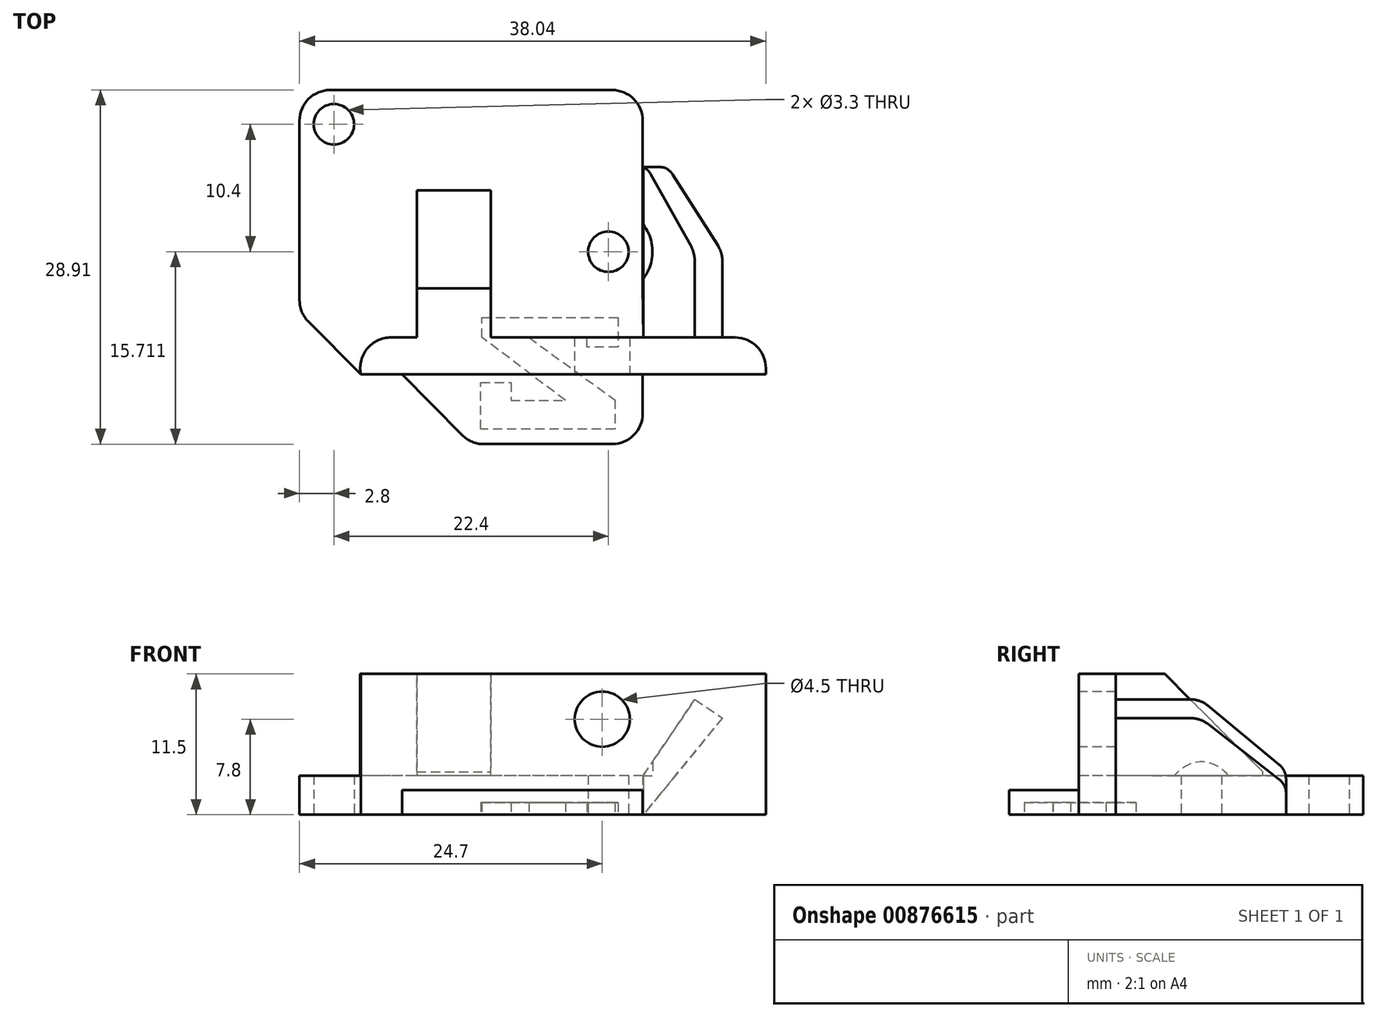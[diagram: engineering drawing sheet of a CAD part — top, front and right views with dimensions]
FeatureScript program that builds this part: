
annotation { "Feature Type Name" : "Feature", "Feature Type Description" : "" }
export const myFeature = defineFeature(function(context is Context, id is Id, definition is map)
    precondition{}
    {
        {
            var Q0;
            Q0=qCreatedBy(makeId("Top.planeOp"),FACE);
            var sketch = newSketch(context, id + "F0", { "sketchPlane" : qUnion([Q0])});
            skLineSegment(sketch, "E0.bottom", {"start": v(0, -51.12) * mm, "end": v(0, 0) * mm});
            skLineSegment(sketch, "E0.top", {"start": v(28, -51.12) * mm, "end": v(28, 0) * mm});
            skLineSegment(sketch, "E0.left", {"start": v(0, -51.12) * mm, "end": v(28, -51.12) * mm});
            skLineSegment(sketch, "E1", {"start": v(28, -35.12) * mm, "end": v(0, -35.12) * mm});
            skCircle(sketch, "E2", {"center": v(2.8, -37.92) * mm, "radius": 1.65 * mm});
            skCircle(sketch, "E3", {"center": v(25.2, -48.32) * mm, "radius": 1.65 * mm});
            skLineSegment(sketch, "E4.top", {"start": v(0, -58.32) * mm, "end": v(28, -58.32) * mm});
            skLineSegment(sketch, "E4.left", {"start": v(0, -51.12) * mm, "end": v(0, -58.32) * mm});
            skLineSegment(sketch, "E5", {"start": v(8.36, -58.32) * mm, "end": v(13.99, -64.03) * mm});
            skLineSegment(sketch, "E6", {"start": v(13.99, -64.03) * mm, "end": v(28, -64.03) * mm});
            skLineSegment(sketch, "E7", {"start": v(28, -64.03) * mm, "end": v(28, -58.32) * mm});
            skLineSegment(sketch, "E8", {"start": v(28.04, -55.32) * mm, "end": v(0, -55.32) * mm});
            skLineSegment(sketch, "E9", {"start": v(28, -51.12) * mm, "end": v(28.04, -55.32) * mm});
            skLineSegment(sketch, "E10", {"start": v(28.04, -55.32) * mm, "end": v(38.04, -55.32) * mm});
            skLineSegment(sketch, "E11", {"start": v(38.04, -55.32) * mm, "end": v(38.04, -58.32) * mm});
            skLineSegment(sketch, "E12", {"start": v(38.04, -58.32) * mm, "end": v(28, -58.32) * mm});
            skSolve(sketch);
        }
        {
            var Q0;
            {var subQ0=sQuery(id+"F0.wireOp",EDGE,"E1");Q0=makeQuery(id+"F0.imprint","IMPRINT",FACE,{"disambiguationData":[TD([[makeQuery(id+"F0.imprint","IMPRINT",EDGE,{"derivedFrom":subQ0}),1.0]])]});}
            var Q1;
            {var subQ0=sQuery(id+"F0.wireOp",EDGE,"E0.left");Q1=makeQuery(id+"F0.imprint","IMPRINT",FACE,{"disambiguationData":[TD([[makeQuery(id+"F0.imprint","IMPRINT",EDGE,{"derivedFrom":subQ0}),-1.0]])]});}
            extrude(context, id + "F1", {"entities" : qUnion([Q0, Q1]), "depth" : 3.2 * mm, "offsetDistance" : 25 * mm});
        }
        {
            var Q0;
            {var subQ3=sQuery(id+"F0.wireOp",EDGE,"E8");Q0=makeQuery(id+"F0.imprint","IMPRINT",FACE,{"disambiguationData":[TD([[makeQuery(id+"F0.imprint","IMPRINT",EDGE,{"derivedFrom":subQ3}),1.0]])]});}
            extrude(context, id + "F2", {"entities" : qUnion([Q0]), "operationType" : NewBodyOperationType.ADD, "depth" : 11.5 * mm, "offsetDistance" : 25 * mm});
        }
        {
            var Q0;
            {var subQ2=sQuery(id+"F0.wireOp",EDGE,"E5");Q0=makeQuery(id+"F0.imprint","IMPRINT",FACE,{"disambiguationData":[TD([[makeQuery(id+"F0.imprint","IMPRINT",EDGE,{"derivedFrom":subQ2}),1.0]])]});}
            extrude(context, id + "F3", {"entities" : qUnion([Q0]), "operationType" : NewBodyOperationType.ADD, "depth" : 2 * mm, "offsetDistance" : 25 * mm});
        }
        {
            var Q0;
            Q0=makeQuery(id+"F2.opExtrude","SWEPT_FACE",FACE,{"disambiguationData":[OSD([sQuery(id+"F0.wireOp",EDGE,"E4.top")])]});
            var sketch = newSketch(context, id + "F4", { "sketchPlane" : qUnion([Q0])});
            skCircle(sketch, "E13", {"center": v(24.7, 7.8) * mm, "radius": 2.25 * mm});
            skSolve(sketch);
        }
        {
            var Q0;
            {var subQ0=sQuery(id+"F4.wireOp",EDGE,"E13");var subQ1=makeQuery(id+"F2.opExtrude","CAP_EDGE",EDGE,{"disambiguationData":[OSD([sQuery(id+"F0.wireOp",EDGE,"E4.top")])],"isStart":false});var subQ2=makeQuery(id+"F4.imprint","INTERSECT",VERTEX,{"disambiguationData":[OD(0.0)],"derivedFrom":[subQ1,subQ0]});Q0=makeQuery(id+"F4.imprint","IMPRINT",FACE,{"disambiguationData":[TD([[makeQuery(id+"F4.imprint","IMPRINT",EDGE,{"disambiguationData":[TD([[subQ2,1.0]])],"derivedFrom":subQ0}),1.0]])]});}
            var Q1;
            {var subQ0=sQuery(id+"F4.wireOp",EDGE,"E13");var subQ1=makeQuery(id+"F2.opExtrude","CAP_EDGE",EDGE,{"disambiguationData":[OSD([sQuery(id+"F0.wireOp",EDGE,"E4.top")])],"isStart":false});var subQ2=makeQuery(id+"F4.imprint","INTERSECT",VERTEX,{"disambiguationData":[OD(0.0)],"derivedFrom":[subQ1,subQ0]});Q1=makeQuery(id+"F4.imprint","IMPRINT",FACE,{"disambiguationData":[TD([[makeQuery(id+"F4.imprint","IMPRINT",EDGE,{"disambiguationData":[TD([[subQ2,-1.0]])],"derivedFrom":subQ0}),1.0]])]});}
            extrude(context, id + "F5", {"entities" : qUnion([Q0, Q1]), "operationType" : NewBodyOperationType.REMOVE, "oppositeDirection" : true, "depth" : 25 * mm, "offsetDistance" : 25 * mm});
        }
        {
            var Q0;
            Q0=makeQuery(id+"F2.opExtrude","SWEPT_EDGE",EDGE,{"disambiguationData":[OSD([sQuery(id+"F0.wireOp",EDGE,"E4.top"),sQuery(id+"F0.wireOp",EDGE,"E4.left")])]});
            chamfer(context, id + "F6", {"entities" : qUnion([Q0]), "width" : 5 * mm, "tangentPropagation" : true});
        }
        {
            var Q0;
            Q0=makeQuery(id+"F6.opChamfer","BLEND_EDGE",EDGE,{"blendedFrom":[makeQuery(id+"F2.opExtrude","SWEPT_EDGE",EDGE,{"disambiguationData":[OSD([sQuery(id+"F0.wireOp",EDGE,"E4.top"),sQuery(id+"F0.wireOp",EDGE,"E4.left")])]}),makeQuery(id+"F2.opExtrude","SWEPT_FACE",FACE,{"disambiguationData":[OSD([sQuery(id+"F0.wireOp",EDGE,"E8")])]})],"blendedInto":[makeQuery(id+"F2.opExtrude","SWEPT_FACE",FACE,{"disambiguationData":[OSD([sQuery(id+"F0.wireOp",EDGE,"E8")])]})]});
            var Q1;
            {var subQ0=sQuery(id+"F0.wireOp",EDGE,"E4.left");Q1=makeQuery(id+"F6.opChamfer","BLEND_EDGE",EDGE,{"blendedFrom":[makeQuery(id+"F2.opExtrude","SWEPT_EDGE",EDGE,{"disambiguationData":[OSD([sQuery(id+"F0.wireOp",EDGE,"E4.top"),subQ0])]}),makeQuery(id+"F2.boolean.opBoolean","MERGE",FACE,{"derivedFrom":[makeQuery(id+"F1.opExtrude","SWEPT_FACE",FACE,{"disambiguationData":[OSD([sQuery(id+"F0.wireOp",EDGE,"E0.bottom"),subQ0])]}),makeQuery(id+"F2.opExtrude","SWEPT_FACE",FACE,{"disambiguationData":[OSD([subQ0])]})]})],"blendedInto":[makeQuery(id+"F2.boolean.opBoolean","MERGE",FACE,{"derivedFrom":[makeQuery(id+"F1.opExtrude","SWEPT_FACE",FACE,{"disambiguationData":[OSD([sQuery(id+"F0.wireOp",EDGE,"E0.bottom"),subQ0])]}),makeQuery(id+"F2.opExtrude","SWEPT_FACE",FACE,{"disambiguationData":[OSD([subQ0])]})]})]});}
            var Q2;
            Q2=makeQuery(id+"F3.opExtrude","SWEPT_EDGE",EDGE,{"disambiguationData":[OSD([sQuery(id+"F0.wireOp",EDGE,"E5"),sQuery(id+"F0.wireOp",EDGE,"E6")])]});
            var Q3;
            Q3=makeQuery(id+"F3.opExtrude","SWEPT_EDGE",EDGE,{"disambiguationData":[OSD([sQuery(id+"F0.wireOp",EDGE,"E6"),sQuery(id+"F0.wireOp",EDGE,"E7")])]});
            var Q4;
            Q4=makeQuery(id+"F1.opExtrude","SWEPT_EDGE",EDGE,{"disambiguationData":[OSD([sQuery(id+"F0.wireOp",EDGE,"E0.top"),sQuery(id+"F0.wireOp",EDGE,"E1")])]});
            var Q5;
            Q5=makeQuery(id+"F1.opExtrude","SWEPT_EDGE",EDGE,{"disambiguationData":[OSD([sQuery(id+"F0.wireOp",EDGE,"E0.bottom"),sQuery(id+"F0.wireOp",EDGE,"E1")])]});
            var Q6;
            Q6=makeQuery(id+"F3.opExtrude","SWEPT_EDGE",EDGE,{"disambiguationData":[OSD([sQuery(id+"F0.wireOp",EDGE,"E4.top"),sQuery(id+"F0.wireOp",EDGE,"E5")])]});
            var Q7;
            Q7=makeQuery(id+"F2.opExtrude","SWEPT_EDGE",EDGE,{"disambiguationData":[OSD([sQuery(id+"F0.wireOp",EDGE,"E10"),sQuery(id+"F0.wireOp",EDGE,"E11")])]});
            fillet(context, id + "F7", {"entities" : qUnion([Q0, Q1, Q2, Q3, Q4, Q5, Q6, Q7]), "radius" : 2.5 * mm, "tangentPropagation" : true, "allowEdgeOverflow" : false});
        }
        {
            var Q0;
            Q0=makeQuery(id+"F2.opExtrude","SWEPT_FACE",FACE,{"disambiguationData":[OSD([sQuery(id+"F0.wireOp",EDGE,"E8"),sQuery(id+"F0.wireOp",EDGE,"E10")])]});
            var sketch = newSketch(context, id + "F8", { "sketchPlane" : qUnion([Q0])});
            skLineSegment(sketch, "E14", {"start": v(-15.6, 3.2) * mm, "end": v(-15.6, 11.5) * mm});
            skLineSegment(sketch, "E15", {"start": v(-15.6, 11.5) * mm, "end": v(-9.57, 11.5) * mm});
            skLineSegment(sketch, "E16", {"start": v(-9.57, 11.5) * mm, "end": v(-9.57, 3.2) * mm});
            skLineSegment(sketch, "E17", {"start": v(-9.57, 3.2) * mm, "end": v(-15.6, 3.2) * mm});
            skLineSegment(sketch, "E18", {"start": v(-28.04, 3.2) * mm, "end": v(-32.25, 9.42) * mm});
            skLineSegment(sketch, "E19", {"start": v(-32.25, 9.42) * mm, "end": v(-34.51, 7.89) * mm});
            skLineSegment(sketch, "E20", {"start": v(-34.51, 7.89) * mm, "end": v(-28.04, 0) * mm});
            skLineSegment(sketch, "E21", {"start": v(-28.04, 0) * mm, "end": v(-28.04, 3.2) * mm});
            skSolve(sketch);
        }
        {
            var Q0;
            Q0=makeQuery(id+"F8.imprint","IMPRINT",FACE,{"disambiguationData":[TD([[makeQuery(id+"F8.imprint","IMPRINT",EDGE,{"derivedFrom":sQuery(id+"F8.wireOp",EDGE,"E14")}),-1.0]])]});
            extrude(context, id + "F9", {"entities" : qUnion([Q0]), "operationType" : NewBodyOperationType.ADD, "depth" : 12 * mm, "offsetDistance" : 25 * mm});
        }
        {
            var Q0;
            Q0=makeQuery(id+"F9.opExtrude","CAP_EDGE",EDGE,{"disambiguationData":[OSD([sQuery(id+"F8.wireOp",EDGE,"E15")])],"isStart":false});
            chamfer(context, id + "F10", {"entities" : qUnion([Q0]), "width" : 8 * mm, "tangentPropagation" : true});
        }
        {
            var Q0;
            Q0=makeQuery(id+"F8.imprint","IMPRINT",FACE,{"disambiguationData":[TD([[makeQuery(id+"F8.imprint","IMPRINT",EDGE,{"derivedFrom":sQuery(id+"F8.wireOp",EDGE,"E18")}),1.0]])]});
            extrude(context, id + "F11", {"entities" : qUnion([Q0]), "operationType" : NewBodyOperationType.ADD, "depth" : 13.9 * mm, "offsetDistance" : 25 * mm});
        }
        {
            var Q0;
            Q0=makeQuery(id+"F11.opExtrude","CAP_EDGE",EDGE,{"disambiguationData":[OSD([sQuery(id+"F8.wireOp",EDGE,"E19")])],"isStart":false});
            chamfer(context, id + "F12", {"entities" : qUnion([Q0]), "width" : 7 * mm, "tangentPropagation" : true});
        }
        {
            var Q0;
            {var subQ0=sQuery(id+"F8.wireOp",EDGE,"E19");Q0=makeQuery(id+"F12.opChamfer","BLEND_EDGE",EDGE,{"blendedFrom":[makeQuery(id+"F11.opExtrude","CAP_EDGE",EDGE,{"disambiguationData":[OSD([subQ0])],"isStart":false}),makeQuery(id+"F11.opExtrude","CAP_FACE",FACE,{"disambiguationData":[OSD([sQuery(id+"F8.wireOp",EDGE,"E18"),subQ0,sQuery(id+"F8.wireOp",EDGE,"E20"),sQuery(id+"F8.wireOp",EDGE,"E21")])],"isStart":false})],"blendedInto":[makeQuery(id+"F11.opExtrude","CAP_FACE",FACE,{"disambiguationData":[OSD([sQuery(id+"F8.wireOp",EDGE,"E18"),subQ0,sQuery(id+"F8.wireOp",EDGE,"E20"),sQuery(id+"F8.wireOp",EDGE,"E21")])],"isStart":false})]});}
            var Q1;
            {var subQ0=sQuery(id+"F8.wireOp",EDGE,"E19");Q1=makeQuery(id+"F12.opChamfer","BLEND_EDGE",EDGE,{"blendedFrom":[makeQuery(id+"F11.opExtrude","CAP_EDGE",EDGE,{"disambiguationData":[OSD([subQ0])],"isStart":false}),makeQuery(id+"F11.opExtrude","SWEPT_FACE",FACE,{"disambiguationData":[OSD([subQ0])]})],"blendedInto":[makeQuery(id+"F11.opExtrude","SWEPT_FACE",FACE,{"disambiguationData":[OSD([subQ0])]})]});}
            var Q2;
            Q2=makeQuery(id+"F11.opExtrude","CAP_EDGE",EDGE,{"disambiguationData":[OSD([sQuery(id+"F8.wireOp",EDGE,"E19")])],"isStart":true});
            fillet(context, id + "F13", {"entities" : qUnion([Q0, Q1, Q2]), "radius" : 2 * mm, "tangentPropagation" : true, "allowEdgeOverflow" : false});
        }
        {
            var Q0;
            Q0=makeQuery(id+"F1.opExtrude","CAP_FACE",FACE,{"disambiguationData":[OSD([sQuery(id+"F0.wireOp",EDGE,"E0.bottom"),sQuery(id+"F0.wireOp",EDGE,"E0.top"),sQuery(id+"F0.wireOp",EDGE,"E1"),sQuery(id+"F0.wireOp",EDGE,"E2"),sQuery(id+"F0.wireOp",EDGE,"E3"),sQuery(id+"F0.wireOp",EDGE,"E4.left"),sQuery(id+"F0.wireOp",EDGE,"E8"),sQuery(id+"F0.wireOp",EDGE,"E9")])],"isStart":false});
            var sketch = newSketch(context, id + "F14", { "sketchPlane" : qUnion([Q0])});
            skCircle(sketch, "E22", {"center": v(25.2, -48.32) * mm, "radius": 3.6 * mm});
            skSolve(sketch);
        }
        {
            var Q0;
            Q0=makeQuery(id+"F14.imprint","IMPRINT",FACE,{"disambiguationData":[TD([[makeQuery(id+"F14.imprint","IMPRINT",EDGE,{"derivedFrom":makeQuery(id+"F1.opExtrude","CAP_EDGE",EDGE,{"disambiguationData":[OSD([sQuery(id+"F0.wireOp",EDGE,"E3")])],"isStart":false})}),-1.0]])]});
            var Q1;
            {var subQ0=sQuery(id+"F14.wireOp",EDGE,"E22");var subQ1=makeQuery(id+"F1.opExtrude","CAP_EDGE",EDGE,{"disambiguationData":[OSD([sQuery(id+"F0.wireOp",EDGE,"E0.top")])],"isStart":false});var subQ2=makeQuery(id+"F14.imprint","INTERSECT",VERTEX,{"disambiguationData":[OD(0.0)],"derivedFrom":[subQ1,subQ0]});Q1=makeQuery(id+"F14.imprint","IMPRINT",FACE,{"disambiguationData":[TD([[makeQuery(id+"F14.imprint","IMPRINT",EDGE,{"disambiguationData":[TD([[subQ2,-1.0]])],"derivedFrom":subQ0}),1.0]])]});}
            extrude(context, id + "F15", {"entities" : qUnion([Q0, Q1]), "operationType" : NewBodyOperationType.REMOVE, "depth" : 10.3 * mm, "offsetDistance" : 25 * mm});
        }
        {
            var Q0;
            {var subQ0=sQuery(id+"F0.wireOp",EDGE,"E1");Q0=makeQuery(id+"F0.imprint","IMPRINT",FACE,{"disambiguationData":[TD([[makeQuery(id+"F0.imprint","IMPRINT",EDGE,{"derivedFrom":subQ0}),1.0]])]});}
            var sketch = newSketch(context, id + "F16", { "sketchPlane" : qUnion([Q0])});
            skLineSegment(sketch, "E23", {"start": v(25.98, -54.06) * mm, "end": v(25.98, -56.1) * mm});
            skLineSegment(sketch, "E24", {"start": v(25.98, -56.1) * mm, "end": v(23.46, -56.1) * mm});
            skLineSegment(sketch, "E25", {"start": v(23.46, -56.1) * mm, "end": v(23.46, -55.32) * mm});
            skLineSegment(sketch, "E26", {"start": v(23.46, -55.32) * mm, "end": v(18.7, -55.32) * mm});
            skLineSegment(sketch, "E27", {"start": v(18.7, -55.32) * mm, "end": v(25.74, -60.41) * mm});
            skLineSegment(sketch, "E28", {"start": v(25.74, -60.41) * mm, "end": v(25.74, -62.79) * mm});
            skLineSegment(sketch, "E29", {"start": v(25.74, -62.79) * mm, "end": v(14.78, -62.79) * mm});
            skLineSegment(sketch, "E30", {"start": v(14.78, -62.79) * mm, "end": v(14.78, -59) * mm});
            skLineSegment(sketch, "E31", {"start": v(14.78, -59) * mm, "end": v(17.25, -59) * mm});
            skLineSegment(sketch, "E32", {"start": v(17.25, -59) * mm, "end": v(17.25, -60.46) * mm});
            skLineSegment(sketch, "E33", {"start": v(17.25, -60.46) * mm, "end": v(21.71, -60.46) * mm});
            skLineSegment(sketch, "E34", {"start": v(21.71, -60.46) * mm, "end": v(14.88, -55.32) * mm});
            skLineSegment(sketch, "E35", {"start": v(14.88, -55.32) * mm, "end": v(14.88, -53.68) * mm});
            skLineSegment(sketch, "E36", {"start": v(14.88, -53.68) * mm, "end": v(25.98, -53.68) * mm});
            skLineSegment(sketch, "E37", {"start": v(25.98, -53.68) * mm, "end": v(25.98, -54.06) * mm});
            skSolve(sketch);
        }
        {
            var Q0;
            Q0=makeQuery(id+"F16.imprint","IMPRINT",FACE,{"disambiguationData":[TD([[makeQuery(id+"F16.imprint","IMPRINT",EDGE,{"derivedFrom":sQuery(id+"F16.wireOp",EDGE,"E23")}),-1.0]])]});
            extrude(context, id + "F17", {"entities" : qUnion([Q0]), "operationType" : NewBodyOperationType.REMOVE, "depth" : 1 * mm, "offsetDistance" : 25 * mm});
        }
    });
